# Revit family: IS_Connect_E7136_BIM_DE
name_source: partatom
category: Plumbing Fixtures
revit_build: Autodesk Revit MEP 2016 (Build: 20161004_0715(x64)
units: mm (PartAtom-declared; Revit-internal decimal feet)

## family parameters
Cut with Voids When Loaded = No
Host = Face
OmniClass Number = 23.45.05.14.14
OmniClass Title = Sinks/Lavatories
Part Type = Normal
Room Calculation Point = No
Round Connector Dimension = Use Diameter
Shared = Yes

## types (2) — shared parameters
Accessories = www.idealstandard.de\ersatzteile
Assembly Code = C1030200
AssetType = Fest
BIMobject category = Basins
Brand url = http://www.idealstandard.de
CodePerformance = DIN EN 14688 CL 10, DIN EN 31
Color = White
CurrencyUnit = €
CurrentRevision = 1
Date of publishing = 15/09/2017
Default Elevation = 850 mm
DurationUnit = Jahr
Edition number = 1
ExpectedLife = 25
Features = CONNECT ARC corner washbasin 480x440mm, 1 taphole, with overflow
Finish = White
IFC Classification = Sanitary Terminal
Installation instructions = http://www.idealstandard.de
InstallationInstructions = www.idealstandard.de\produkte
MainColor = White
Manufacturer = www.idealstandard.de\produkte
Manufacturer name = Ideal Standard
ManufacturerURL = http://www.idealstandard.de
Material = Vitreous china
Material main = Vitreous china
NettWeight = 9,9 kg
Nominal height = 157 mm
Nominal width = 381 mm
Product Guid = d9036d60-47b7-4ae6-81f3-2c1ecc6a130a
Product SKU = E7136
Product data url = https://bimobject.com
Product family = Sanitary
Product group = Wash basin systems
Product url = http://www.idealstandard.de
ProductInformation = www.idealstandard.de\produkte
QR code = http://bimobject.com
Shape = Sculptured
Space = Intern
SpareParts = www.idealstandard.de/ersatzteile
Technical description = http://www.idealstandard.de
URL = http://www.idealstandard.de
Uniclass 2.0 Code = SS-35-65-70-94
Uniclass 2.0 Description = Wash Basin Systems
Uniclass 2015 Code = Ss_40_15_75_94
Uniclass 2015 Name = Wash basin systems
Uniclass2015Code = Pr_40_20_96_96
Uniclass2015Title = Wall-hung wash basins
Uniclass2015Version = Products v1.1
Version = 1
VolumeUnits = Litres
WasteCover = ISI_IdealStandard_BasinMaterial_White3_Render
Weight Net (Kg) = 9.9
zero-valued in all types: CWFU, Cost, DrainSize, HWFU, WFU

## per-type parameters (varying)
| type | BarCode | Description | EAN code | Model | ModelNumber | ModelReference |
| E713601 - CONNECT ARC LAVABO ANG. 45 1F BEU | 5017830399667 | E713601 CONNECT ARC corner washbasin 480x440mm, 1 taphole, with overflow | https://5017830399667 | E713601 | E713601 | E713601 CONNECT ARC corner washbasin 480x440mm, 1 taphole, with overflow |
| E7136MA - CONNECT ARC LAVABO ANG. 45 1F BEU with Ideal Plus | 5017830399650 | E7136MA CONNECT ARC corner washbasin 480x440mm, 1 taphole, with overflow with Ideal Plus | https://5017830399650 | E7136MA | E7136MA | E71336MA CONNECT ARC corner washbasin 480x440mm, 1 taphole, with overflow with Ideal Plus |

## geometry (parser evidence)
native form markers: Blend x8, Sweep x2
no freeform markers — native parametric forms only
